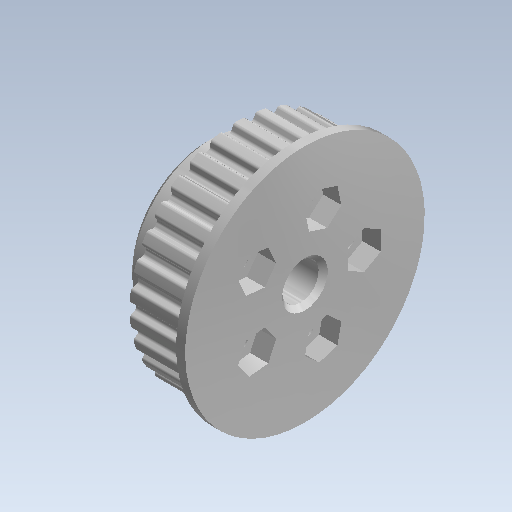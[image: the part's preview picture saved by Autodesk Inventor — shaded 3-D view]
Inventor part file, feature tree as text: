
AUTODESK INVENTOR PART (.ipt)
format: ipt  version: 2020 (Build 240168000, 168)  size: 1,547,776 bytes
history: native  units: mm (DEFAULTED — no unit token found)
features: extrude x10, sketch x10, projected_geometry x6, plane x5, chamfer x3, other x3, thicken_offset x2, pattern_circular x2, fillet x2, revolve x1, hole x1, reference x1
ambient origin geometry x8: Origin, YZ Plane, XZ Plane, XY Plane, X Axis, Y Axis, Z Axis, Center Point
bodies: Solid1 (feature_tree)
feature tree (46):
  revolve  "Revolution1"  [1 undecoded]
  hole  "Hole1"  [1 undecoded]
  extrude  "Extrusion1"  TaperAngle=0.0deg  [1 undecoded]
  plane  "Work Plane1"
  extrude  "Extrusion2"  Depth=5.0mm TaperAngle=0.0deg
  plane  "Work Plane2"
  extrude  "Extrusion3"  Depth=10.0mm TaperAngle=0.0deg
  extrude  "Extrusion5"  Depth=10.0mm
  sketch  "Sketch8"  dims[d15=70.0mm d16=5.0mm d17=0.0mm]
  plane  "Work Plane3"
  extrude  "Extrusion6"  Depth=10.0mm
  sketch  "Sketch9"  dims[d25=8.0mm d26=10.0mm d27=0.0mm]
  plane  "Work Plane4"
  extrude  "Extrusion7"  Depth=10.0mm
  sketch  "Sketch10"  dims[d28=10.0mm d29=0.0mm d30=34.85mm]
  plane  "Work Plane5"
  extrude  "Extrusion8"  Depth=4.0mm
  thicken_offset  "Thicken1"
  extrude  "Extrusion9"  Depth=4.0mm
  extrude  "Extrusion10"  Depth=10.0mm TaperAngle=0.0deg
  pattern_circular  "Circular Pattern2"  [2 undecoded]
  thicken_offset  "Thicken2"
  extrude  "Extrusion11"  TaperAngle=30.0deg  [1 undecoded]
  fillet  "Fillet1"  Radius=60.0mm
  pattern_circular  "Circular Pattern3"  [2 undecoded]
  fillet  "Fillet2"  Radius=50.0mm
  chamfer  "Chamfer1"  Distance=0.7mm
  chamfer  "Chamfer2"  Distance=15.0mm
  chamfer  "Chamfer3"  Distance=28.0mm
  sketch  "Sketch2"  dims[d0=360.0deg]
  sketch  "Sketch4"  dims[d1=10.0mm d2=6.0mm d3=4.0mm d4=2.0mm d5=90.0deg d6=12.5mm d7=0.0mm d8=7.5mm d9=0.0mm]
  sketch  "Sketch5"  dims[d10=0.0mm d11=70.0mm]
  sketch  "Sketch7"  dims[d12=5.0mm d13=0.0mm d14=0.0mm]
  projected_geometry  "Projected Loop2"
  projected_geometry  "Projected Loop3"
  reference  "Reference1"
  projected_geometry  "Projected Loop4"
  sketch  "Sketch11"  dims[d31=10.0mm d32=0.0mm d33=54.0mm]
  projected_geometry  "Projected Loop5"
  sketch  "Sketch12"  dims[d34=10.0mm d35=0.0mm d36=2.0mm]
  projected_geometry  "Projected Loop6"
  sketch  "Sketch13"  dims[d37=2.0mm d38=13.0mm d39=4.2mm d40=10.0mm d41=0.0mm d42=4.2mm d43=30.0deg d44=60.0mm d46=360.0deg d48=4.0mm d49=0.0mm d50=50.0mm d51=360.0deg d53=0.7mm d54=1.0mm d55=15.0mm d56=28.0mm d57=3.141593mm d58=3.141593mm d59=14.0mm d60=0.0mm d61=1.0mm d62=50.0mm d63=360.0deg d65=2.0mm d66=1.0mm d67=2.0mm d68=45.0deg d69=1.0mm d70=2.0mm d71=45.0deg d72=1.0mm d73=2.0mm d74=45.0deg]
  projected_geometry  "Projected Loop7"
  parser-record x1  (decoder bookkeeping rows leaked as tree rows — omitted from the tree; the rows remain in map.json)
  other  "reducer_leg.iam"
  other  "bearing_35_44_5:1"
note: 8 required parameter values undecoded (feature->parameter linkage not recoverable at this tier; creation-order binding heuristic only, values carry confidence <= 0.55)
note: 1 file-system path scrubbed to <path> (originals preserved in map.json)